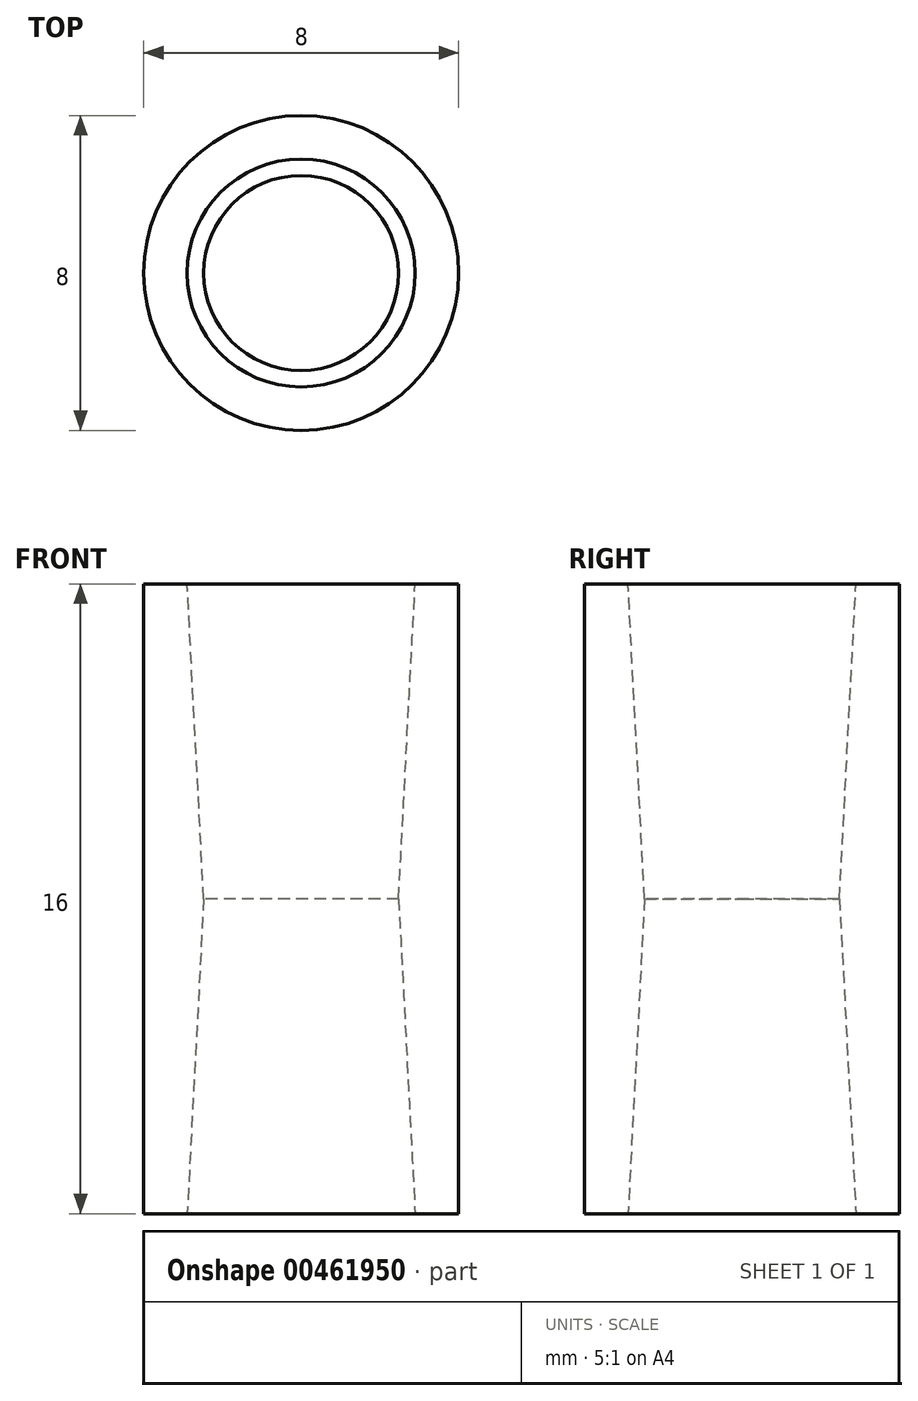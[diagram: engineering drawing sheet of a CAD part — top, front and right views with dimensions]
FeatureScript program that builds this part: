
annotation { "Feature Type Name" : "Feature", "Feature Type Description" : "" }
export const myFeature = defineFeature(function(context is Context, id is Id, definition is map)
    precondition{}
    {
        {
            var Q0;
            Q0=qCreatedBy(makeId("Top.planeOp"),FACE);
            var sketch = newSketch(context, id + "F0", { "sketchPlane" : qUnion([Q0])});
            skCircle(sketch, "E0", {"center": v(0, 0) * mm, "radius": 4 * mm});
            skCircle(sketch, "E1.0", {"center": v(0, 0) * mm, "radius": 2.48 * mm});
            skSolve(sketch);
        }
        {
            assignVariable(context, id + "F1", {"name" : "wrist_brg_len", "anyValue" : 8 * mm});
        }
        {
            var Q0;
            Q0 = qSketchRegion(id + "F0", true);
            var Q1;
            Q1=makeQuery(id+"F0.imprint","IMPRINT",FACE,{"disambiguationData":[TD([[makeQuery(id+"F0.imprint","IMPRINT",EDGE,{"derivedFrom":sQuery(id+"F0.wireOp",EDGE,"E1.0")}),1.0]])]});
            extrude(context, id + "F2", {"entities" : qUnion([Q0, Q1]), "depth" : getVariable(context, 'wrist_brg_len') * 2, "symmetric" : true});
        }
        {
            var Q0;
            Q0=makeQuery(id+"F0.imprint","IMPRINT",FACE,{"disambiguationData":[TD([[makeQuery(id+"F0.imprint","IMPRINT",EDGE,{"derivedFrom":sQuery(id+"F0.wireOp",EDGE,"E1.0")}),1.0]])]});
            extrude(context, id + "F3", {"entities" : qUnion([Q0]), "operationType" : NewBodyOperationType.REMOVE, "depth" : 25.4 * mm, "hasDraft" : true, "draftAngle" : 3 * degree, "hasSecondDirectionDraft" : true, "secondDirectionDraftAngle" : 3 * degree, "symmetric" : true});
        }
    });
